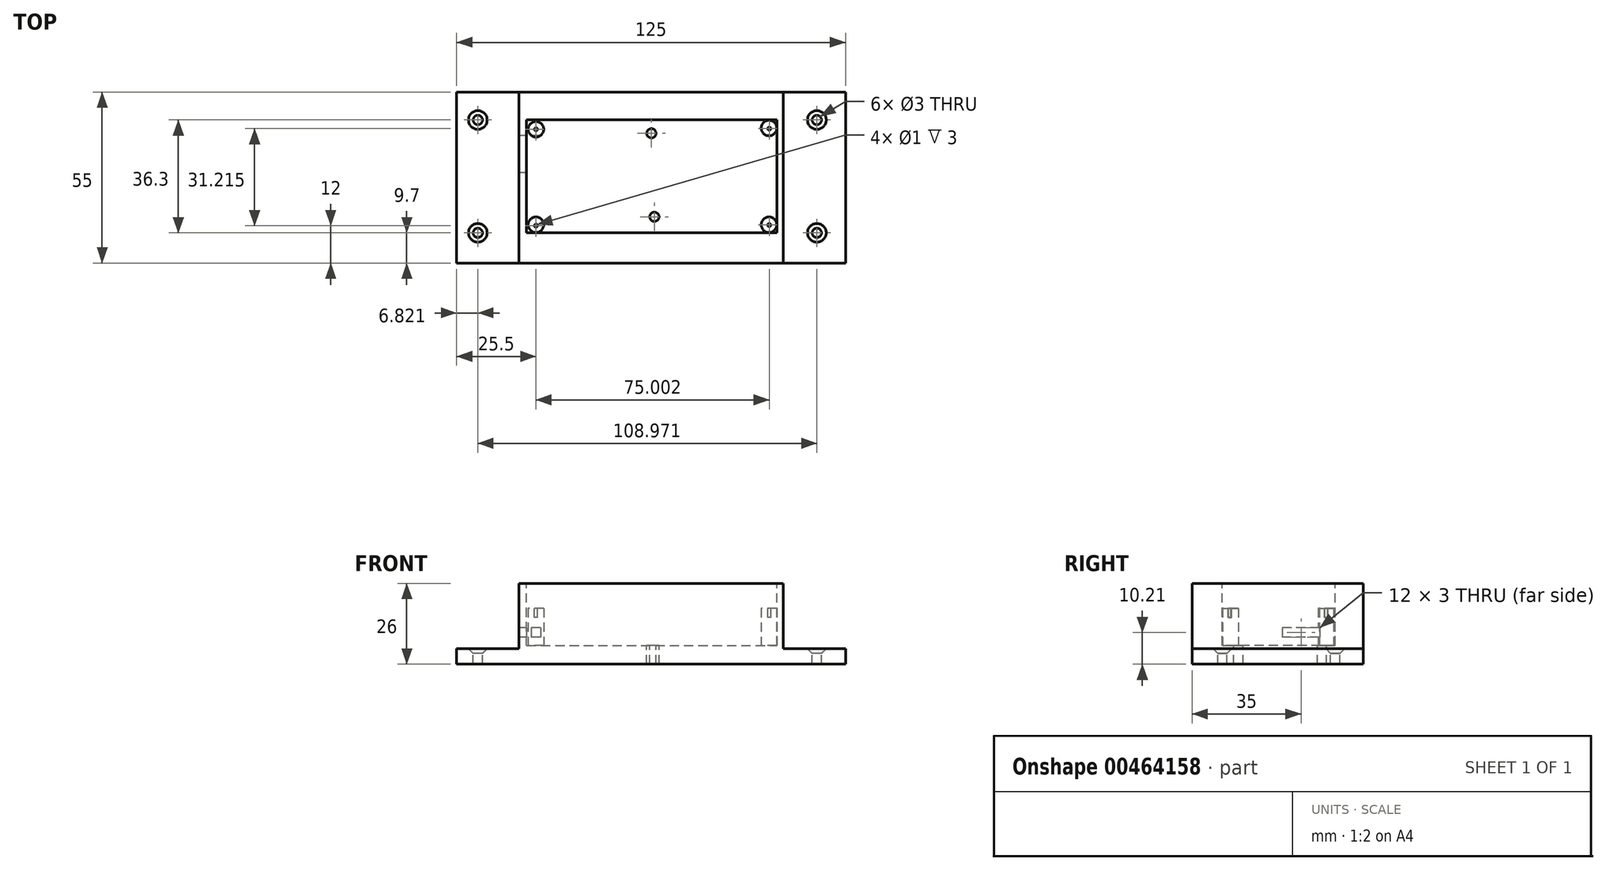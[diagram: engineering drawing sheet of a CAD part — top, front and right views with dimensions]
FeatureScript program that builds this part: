
annotation { "Feature Type Name" : "Feature", "Feature Type Description" : "" }
export const myFeature = defineFeature(function(context is Context, id is Id, definition is map)
    precondition{}
    {
        {
            var Q0;
            Q0=qCreatedBy(makeId("Top.planeOp"),FACE);
            var sketch = newSketch(context, id + "F0", { "sketchPlane" : qUnion([Q0])});
            skLineSegment(sketch, "E0.bottom", {"start": v(0, 0) * mm, "end": v(125, 0) * mm});
            skLineSegment(sketch, "E0.top", {"start": v(0, 55) * mm, "end": v(125, 55) * mm});
            skLineSegment(sketch, "E0.left", {"start": v(0, 0) * mm, "end": v(0, 55) * mm});
            skLineSegment(sketch, "E0.right", {"start": v(125, 0) * mm, "end": v(125, 55) * mm});
            skSolve(sketch);
        }
        {
            var Q0;
            Q0 = qSketchRegion(id + "F0", true);
            extrude(context, id + "F1", {"entities" : qUnion([Q0]), "depth" : 5 * mm, "offsetDistance" : 25 * mm});
        }
        {
            var Q0;
            Q0=makeQuery(id+"F1.opExtrude","CAP_FACE",FACE,{"disambiguationData":[OSD([sQuery(id+"F0.wireOp",EDGE,"E0.bottom"),sQuery(id+"F0.wireOp",EDGE,"E0.top"),sQuery(id+"F0.wireOp",EDGE,"E0.left"),sQuery(id+"F0.wireOp",EDGE,"E0.right")])],"isStart":false});
            var sketch = newSketch(context, id + "F2", { "sketchPlane" : qUnion([Q0])});
            skLineSegment(sketch, "E1.bottom", {"start": v(20, 55) * mm, "end": v(105, 55) * mm});
            skLineSegment(sketch, "E1.top", {"start": v(20, 0) * mm, "end": v(105, 0) * mm});
            skLineSegment(sketch, "E1.left", {"start": v(20, 55) * mm, "end": v(20, 0) * mm});
            skLineSegment(sketch, "E1.right", {"start": v(105, 55) * mm, "end": v(105, 0) * mm});
            skSolve(sketch);
        }
        {
            var Q0;
            Q0 = qSketchRegion(id + "F2", true);
            extrude(context, id + "F3", {"entities" : qUnion([Q0]), "operationType" : NewBodyOperationType.ADD, "depth" : 21 * mm, "offsetDistance" : 25 * mm});
        }
        {
            var Q0;
            Q0=makeQuery(id+"F3.opExtrude","CAP_FACE",FACE,{"disambiguationData":[OSD([sQuery(id+"F2.wireOp",EDGE,"E1.bottom"),sQuery(id+"F2.wireOp",EDGE,"E1.top"),sQuery(id+"F2.wireOp",EDGE,"E1.left"),sQuery(id+"F2.wireOp",EDGE,"E1.right")])],"isStart":false});
            var sketch = newSketch(context, id + "F4", { "sketchPlane" : qUnion([Q0])});
            skLineSegment(sketch, "E2.bottom", {"start": v(22.5, 46) * mm, "end": v(103, 46) * mm});
            skLineSegment(sketch, "E2.top", {"start": v(22.5, 9.7) * mm, "end": v(103, 9.7) * mm});
            skLineSegment(sketch, "E2.left", {"start": v(22.5, 46) * mm, "end": v(22.5, 9.7) * mm});
            skLineSegment(sketch, "E2.right", {"start": v(103, 46) * mm, "end": v(103, 9.7) * mm});
            skSolve(sketch);
        }
        {
            var Q0;
            Q0 = qSketchRegion(id + "F4", true);
            extrude(context, id + "F5", {"entities" : qUnion([Q0]), "operationType" : NewBodyOperationType.REMOVE, "oppositeDirection" : true, "depth" : 20 * mm, "offsetDistance" : 25 * mm});
        }
        {
            var Q0;
            Q0=makeQuery(id+"F5.boolean.opBoolean","COPY",FACE,{"derivedFrom":makeQuery(id+"F5.opExtrude","CAP_FACE",FACE,{"disambiguationData":[OSD([sQuery(id+"F4.wireOp",EDGE,"E2.bottom"),sQuery(id+"F4.wireOp",EDGE,"E2.top"),sQuery(id+"F4.wireOp",EDGE,"E2.left"),sQuery(id+"F4.wireOp",EDGE,"E2.right")])],"isStart":false})});
            var sketch = newSketch(context, id + "F6", { "sketchPlane" : qUnion([Q0])});
            skCircle(sketch, "E3", {"center": v(25.5, 43) * mm, "radius": 2.5 * mm});
            skCircle(sketch, "E4", {"center": v(100.4, 43.4) * mm, "radius": 2.5 * mm});
            skCircle(sketch, "E5", {"center": v(100.4, 12.3) * mm, "radius": 2.5 * mm});
            skCircle(sketch, "E6", {"center": v(25.5, 12.3) * mm, "radius": 2.5 * mm});
            skSolve(sketch);
        }
        {
            var Q0;
            Q0 = qSketchRegion(id + "F6", true);
            extrude(context, id + "F7", {"entities" : qUnion([Q0]), "operationType" : NewBodyOperationType.ADD, "depth" : 12 * mm, "offsetDistance" : 25 * mm});
        }
        {
            var Q0;
            Q0=makeQuery(id+"F3.opExtrude","SWEPT_FACE",FACE,{"disambiguationData":[OSD([sQuery(id+"F2.wireOp",EDGE,"E1.left")])]});
            var sketch = newSketch(context, id + "F8", { "sketchPlane" : qUnion([Q0])});
            skLineSegment(sketch, "E7.bottom", {"start": v(-41, 11.7) * mm, "end": v(-29, 11.7) * mm});
            skLineSegment(sketch, "E7.top", {"start": v(-41, 8.7) * mm, "end": v(-29, 8.7) * mm});
            skLineSegment(sketch, "E7.left", {"start": v(-41, 11.7) * mm, "end": v(-41, 8.7) * mm});
            skLineSegment(sketch, "E7.right", {"start": v(-29, 11.7) * mm, "end": v(-29, 8.7) * mm});
            skSolve(sketch);
        }
        {
            var Q0;
            Q0 = qSketchRegion(id + "F8", true);
            extrude(context, id + "F9", {"entities" : qUnion([Q0]), "operationType" : NewBodyOperationType.REMOVE, "oppositeDirection" : true, "depth" : 25 * mm, "offsetDistance" : 25 * mm});
        }
        {
            var Q0;
            Q0=makeQuery(id+"F7.opExtrude","CAP_FACE",FACE,{"disambiguationData":[OSD([sQuery(id+"F6.wireOp",EDGE,"E3")])],"isStart":false});
            var sketch = newSketch(context, id + "F10", { "sketchPlane" : qUnion([Q0])});
            skCircle(sketch, "E8", {"center": v(25.5, 43) * mm, "radius": 0.5 * mm});
            skCircle(sketch, "E9", {"center": v(25.5, 12) * mm, "radius": 0.5 * mm});
            skCircle(sketch, "E10", {"center": v(100.5, 43.21) * mm, "radius": 0.5 * mm});
            skCircle(sketch, "E11", {"center": v(100.5, 12.21) * mm, "radius": 0.5 * mm});
            skSolve(sketch);
        }
        {
            var Q0;
            Q0 = qSketchRegion(id + "F10", true);
            extrude(context, id + "F11", {"entities" : qUnion([Q0]), "operationType" : NewBodyOperationType.REMOVE, "oppositeDirection" : true, "depth" : 3 * mm, "offsetDistance" : 25 * mm});
        }
        {
            var Q0;
            Q0=makeQuery(id+"F5.boolean.opBoolean","COPY",FACE,{"derivedFrom":makeQuery(id+"F5.opExtrude","CAP_FACE",FACE,{"disambiguationData":[OSD([sQuery(id+"F4.wireOp",EDGE,"E2.bottom"),sQuery(id+"F4.wireOp",EDGE,"E2.top"),sQuery(id+"F4.wireOp",EDGE,"E2.left"),sQuery(id+"F4.wireOp",EDGE,"E2.right")])],"isStart":false})});
            var sketch = newSketch(context, id + "F12", { "sketchPlane" : qUnion([Q0])});
            skCircle(sketch, "E12", {"center": v(62.6, 41.7) * mm, "radius": 1.5 * mm});
            skCircle(sketch, "E13", {"center": v(63.57, 14.84) * mm, "radius": 1.5 * mm});
            skCircle(sketch, "E14", {"center": v(6.82, 46) * mm, "radius": 1.5 * mm});
            skCircle(sketch, "E15", {"center": v(6.82, 9.7) * mm, "radius": 1.5 * mm});
            skCircle(sketch, "E16", {"center": v(115.8, 46) * mm, "radius": 1.5 * mm});
            skCircle(sketch, "E17", {"center": v(115.8, 9.7) * mm, "radius": 1.5 * mm});
            skSolve(sketch);
        }
        {
            var Q0;
            Q0 = qSketchRegion(id + "F12", true);
            extrude(context, id + "F13", {"entities" : qUnion([Q0]), "operationType" : NewBodyOperationType.REMOVE, "oppositeDirection" : true, "depth" : 25 * mm, "offsetDistance" : 25 * mm});
        }
        {
            var Q0;
            {var subQ0=sQuery(id+"F0.wireOp",EDGE,"E0.left");var subQ1=sQuery(id+"F0.wireOp",EDGE,"E0.top");var subQ2=sQuery(id+"F0.wireOp",EDGE,"E0.bottom");Q0=makeQuery(id+"F13.boolean.opBoolean","INTERSECT",EDGE,{"derivedFrom":[makeQuery(id+"F3.boolean.opBoolean","SPLIT",FACE,{"disambiguationData":[TD([makeQuery(id+"F1.opExtrude","SWEPT_FACE",FACE,{"disambiguationData":[OSD([subQ0])]})])],"derivedFrom":makeQuery(id+"F1.opExtrude","CAP_FACE",FACE,{"disambiguationData":[OSD([subQ2,subQ1,subQ0,sQuery(id+"F0.wireOp",EDGE,"E0.right")])],"isStart":false})}),makeQuery(id+"F13.opExtrude","SWEPT_FACE",FACE,{"disambiguationData":[OSD([sQuery(id+"F12.wireOp",EDGE,"E14")])]})]});}
            var Q1;
            {var subQ0=sQuery(id+"F0.wireOp",EDGE,"E0.left");var subQ1=sQuery(id+"F0.wireOp",EDGE,"E0.top");var subQ2=sQuery(id+"F0.wireOp",EDGE,"E0.bottom");Q1=makeQuery(id+"F13.boolean.opBoolean","INTERSECT",EDGE,{"derivedFrom":[makeQuery(id+"F3.boolean.opBoolean","SPLIT",FACE,{"disambiguationData":[TD([makeQuery(id+"F1.opExtrude","SWEPT_FACE",FACE,{"disambiguationData":[OSD([subQ0])]})])],"derivedFrom":makeQuery(id+"F1.opExtrude","CAP_FACE",FACE,{"disambiguationData":[OSD([subQ2,subQ1,subQ0,sQuery(id+"F0.wireOp",EDGE,"E0.right")])],"isStart":false})}),makeQuery(id+"F13.opExtrude","SWEPT_FACE",FACE,{"disambiguationData":[OSD([sQuery(id+"F12.wireOp",EDGE,"E15")])]})]});}
            var Q2;
            {var subQ0=sQuery(id+"F0.wireOp",EDGE,"E0.top");var subQ1=sQuery(id+"F0.wireOp",EDGE,"E0.right");var subQ2=sQuery(id+"F0.wireOp",EDGE,"E0.bottom");Q2=makeQuery(id+"F13.boolean.opBoolean","INTERSECT",EDGE,{"derivedFrom":[makeQuery(id+"F3.boolean.opBoolean","SPLIT",FACE,{"disambiguationData":[TD([makeQuery(id+"F1.opExtrude","SWEPT_FACE",FACE,{"disambiguationData":[OSD([subQ1])]})])],"derivedFrom":makeQuery(id+"F1.opExtrude","CAP_FACE",FACE,{"disambiguationData":[OSD([subQ2,subQ0,sQuery(id+"F0.wireOp",EDGE,"E0.left"),subQ1])],"isStart":false})}),makeQuery(id+"F13.opExtrude","SWEPT_FACE",FACE,{"disambiguationData":[OSD([sQuery(id+"F12.wireOp",EDGE,"E17")])]})]});}
            var Q3;
            {var subQ0=sQuery(id+"F0.wireOp",EDGE,"E0.top");var subQ1=sQuery(id+"F0.wireOp",EDGE,"E0.right");var subQ2=sQuery(id+"F0.wireOp",EDGE,"E0.bottom");Q3=makeQuery(id+"F13.boolean.opBoolean","INTERSECT",EDGE,{"derivedFrom":[makeQuery(id+"F3.boolean.opBoolean","SPLIT",FACE,{"disambiguationData":[TD([makeQuery(id+"F1.opExtrude","SWEPT_FACE",FACE,{"disambiguationData":[OSD([subQ1])]})])],"derivedFrom":makeQuery(id+"F1.opExtrude","CAP_FACE",FACE,{"disambiguationData":[OSD([subQ2,subQ0,sQuery(id+"F0.wireOp",EDGE,"E0.left"),subQ1])],"isStart":false})}),makeQuery(id+"F13.opExtrude","SWEPT_FACE",FACE,{"disambiguationData":[OSD([sQuery(id+"F12.wireOp",EDGE,"E16")])]})]});}
            var Q4;
            Q4=makeQuery(id+"F13.boolean.opBoolean","COPY",EDGE,{"derivedFrom":makeQuery(id+"F13.opExtrude","CAP_EDGE",EDGE,{"disambiguationData":[OSD([sQuery(id+"F12.wireOp",EDGE,"E12")])],"isStart":true})});
            var Q5;
            Q5=makeQuery(id+"F13.boolean.opBoolean","COPY",EDGE,{"derivedFrom":makeQuery(id+"F13.opExtrude","CAP_EDGE",EDGE,{"disambiguationData":[OSD([sQuery(id+"F12.wireOp",EDGE,"E13")])],"isStart":true})});
            chamfer(context, id + "F14", {"entities" : qUnion([Q0, Q1, Q2, Q3, Q4, Q5]), "width" : 1.5 * mm, "tangentPropagation" : true});
        }
    });
